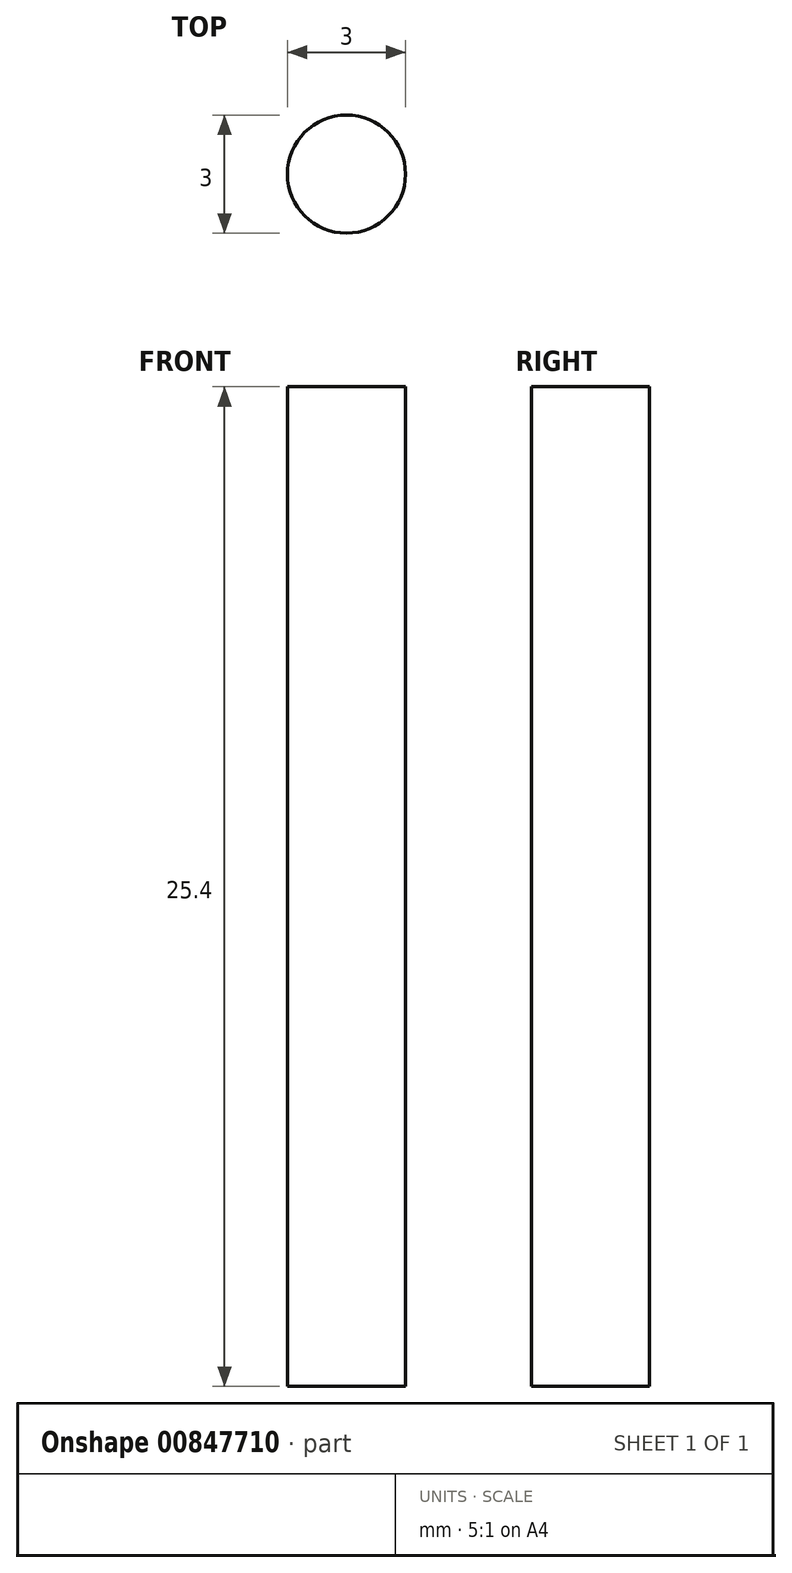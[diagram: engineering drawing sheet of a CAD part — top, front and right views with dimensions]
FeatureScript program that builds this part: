
annotation { "Feature Type Name" : "Feature", "Feature Type Description" : "" }
export const myFeature = defineFeature(function(context is Context, id is Id, definition is map)
    precondition{}
    {
        {
            var Q0;
            Q0=qCreatedBy(makeId("Top.planeOp"),FACE);
            var sketch = newSketch(context, id + "F0", { "sketchPlane" : qUnion([Q0])});
            skCircle(sketch, "E0", {"center": v(0, 0) * mm, "radius": 1.5 * mm});
            skSolve(sketch);
        }
        {
            var Q0;
            Q0 = qSketchRegion(id + "F0", true);
            extrude(context, id + "F1", {"entities" : qUnion([Q0]), "depth" : 25.4 * mm, "offsetDistance" : 25.4 * mm});
        }
    });
